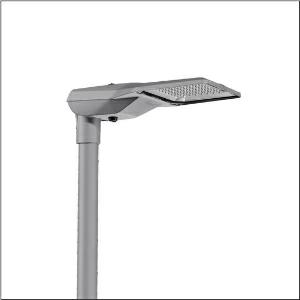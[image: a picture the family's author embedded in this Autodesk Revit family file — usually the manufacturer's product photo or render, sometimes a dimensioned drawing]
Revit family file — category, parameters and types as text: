
# Revit family: streetlight_sl_21_iq_midi___st0_5a_5xe3b31y08nb_abd3
name_source: partatom
category: Lighting Fixtures
units: mm (PartAtom-declared; Revit-internal decimal feet)

## family parameters
Cut with Voids When Loaded = No
Host = Face
Light Source = No
Part Type = Normal
Room Calculation Point = No
Round Connector Dimension = Use Diameter
Shared = No

## types (1)
- --- (1 x LED, 21550 lm, 136.6 W, 3000K)
    Apparent Load = 137 VA
    CIE Flux Codes = 43 76 97 100 100
    Color Rendering = 70
    Color Temperature = 3000K
    Default Elevation = 1800 mm
    Description = Streetlight SL 21 iQ midi, mast luminaire, primary light control with lens, of PMMA, primary optical cover: cover, of toughened safety glass, transparent, light distribution: ST0.5a, light emission: direct distribution, primary light characteristic: asymmetric, installation type: post-top, side-entry, LED, High Power LED, rated luminous flux: 21.550lm, luminous efficacy: 158lm/W, light colour: 730, colour temperature: 3000K, control: presetting dimming logarithmic, Street-Remote, Auto-Match, Temp-Guard, Lumen-Switch, Night-Set, Smart-Wire, Light-Fading, Desk-Remote (wireless, voltage-free reading and setting of iQ features in the workshop via application-optimized NFC function/RFID function), optimised constant luminous flux control (CLO 2.0), mains connection: 230..240V, AC, 50/60Hz, start of lifetime: 137W, end of service life: 144W, reduction: 61W, luminaire housing, of diecast aluminium, powder-coated, Siteco® metallic grey (DB 702S), corrosivity category C5 mid according to DIN EN ISO 12944, please order mast flange separately, inclination adjustable: 0°, 5°, 10°, 15°, sealing non-destructively replaceable, multi-level sealing system, length: 644mm, width: 335mm, height: 110mm, mast flange for spigot size: 42mm (side-entry): 5XC10008XM4, 60/48mm (side-entry/post-top): 5XC10108XM2, 76/60mm (side-entry/post-top): 5XC10108XM1, Smart Interface below and above, protection rating (complete): IP66, insulation class (complete): insulation class II (safety insulation), certification: CE, ENEC, ENEC+, VDE, impact resistance: IK09, permissible operating ambient temperature for outdoor applications: -40..+50°C, standard-compliant lighting for roads and squares, packaging unit: 1 piece

Light Distribution: ST0.5a
    Height = 111 mm
    Lamp = 1 x LED
    Lamp Light Flux = 21550 lm
    Lamp Power = 136.6 W
    Lamp count = 1
    Length = 644 mm
    Luminous efficacy = 158 lm/W
    Manufacturer = Siteco
    ModVariant = No
    Model = 5XE3B31Y08NB
    Number of Poles = 1
    OnlyDefault = Yes
    Power Factor = 1
    Product Name = Streetlight SL 21 iQ midi | ST0.5a
    Product group = mast luminaire | pylon top
    ProductGroupID = 6100
    Protection Class = Protection class II
    Protection Degree = IP 66
    RLX_Detail_Level = 1
    RLX_Emergency_Light_Flux = 0 lm
    RLX_Emergency_Type = 0
    RLX_Emergency_Type_DB = No
    RlxData = <blob elided: 102741 chars, md5=205a03e5>
    Socket = socket
    Standby Power = 0 W
    System Light Flux = 21550 lm
    System Power = 137 W
    Type Comments = factory setting: luminous flux: 100 % | dim-lin: 254 | 733 mA
    Type Image = l_1004304.jpg
    URL = http://relux.com
    VarID = @adj_045837
    Voltage = 0 V
    Weight = 0.00 kg
    Width = 336 mm

## geometry (parser evidence)
native form markers: Blend x4, Sweep x9
no freeform markers — native parametric forms only
